# Revit family: Exterior_-_Commercial_-_Storefront_Entry_w_Sidelights_10928 (1)
name_source: partatom
category: Doors
units: mm (PartAtom-declared; Revit-internal decimal feet)

## family parameters
Always vertical = Yes
Cut with Voids When Loaded = No
Host = Wall
OmniClass Number = 23.30.10.00
OmniClass Title = Doors
Room Calculation Point = No
Shared = No

## types (6) — shared parameters
Analytic Construction = <None>
Define Thermal Properties by = Schematic Type
Frame Height = 6' - 10"
Frame Projection Ext. = 0' - 1"
Frame Projection Int. = 0' - 1"
Frame Width = 0' - 3"
Function = Exterior
Handle = Metal - Handle
Height = 7' - 0"
Wall Closure = By host

## per-type parameters (varying)
| type | Door Width | Rough Height | Rough Width | Swing Radius | Thickness | Width |
| 1 1/2" Thick - 30"W x 82"H | 2' - 0" | 0' - 0" | 0' - 0" | 1' - 10 1/2" | 0' - 1 1/2" | 5' - 0" |
| 1 1/2" Thick - 36"W x 82"H | 3' - 0" | 7' - 0" | 8' - 0" | 2' - 10 1/2" | 0' - 1 1/2" | 8' - 0" |
| 1 3/4" Thick - 30"W x 82"H | 2' - 0" | 0' - 0" | 0' - 0" | 1' - 10 1/2" | 0' - 1 3/4" | 5' - 0" |
| 1 3/4" Thick - 36"W x 82"H | 2' - 6" | 0' - 0" | 8' - 0" | 2' - 4 1/2" | 0' - 1 3/4" | 5' - 6" |
| 2" Thick - 30"W x 82"H | 2' - 0" | 0' - 0" | 0' - 0" | 1' - 10 1/2" | 0' - 2" | 5' - 0" |
| 2" Thick - 36"W x 82"H | 2' - 6" | 0' - 0" | 0' - 0" | 2' - 4 1/2" | 0' - 2" | 5' - 6" |

## geometry (parser evidence)
native form markers: Blend x4, Sweep x1
no freeform markers — native parametric forms only
